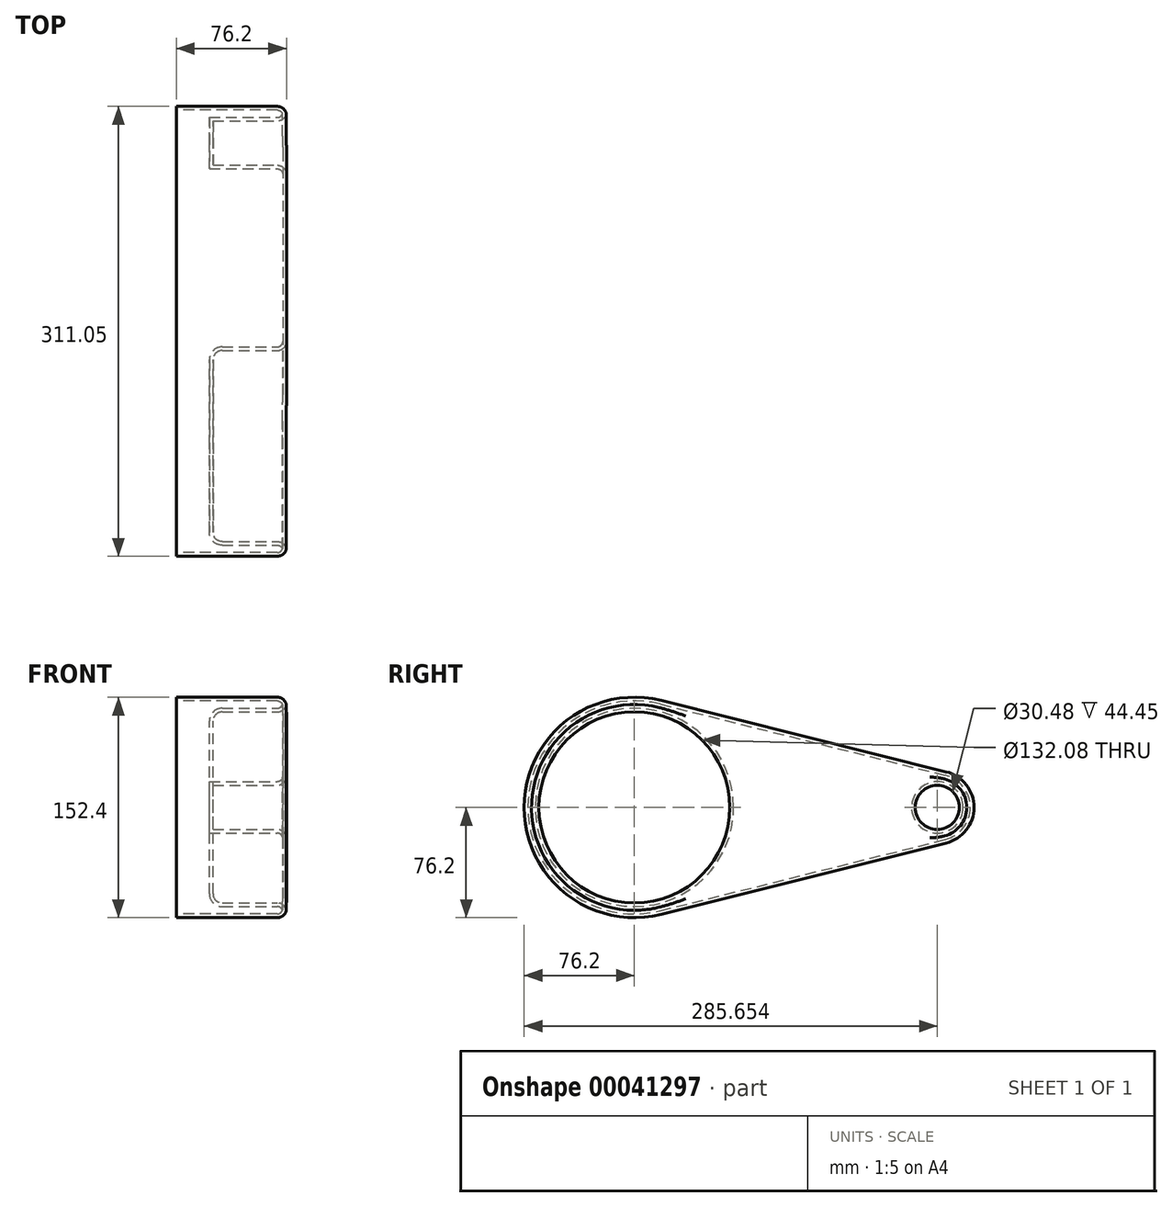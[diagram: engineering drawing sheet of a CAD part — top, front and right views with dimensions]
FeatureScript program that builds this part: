
annotation { "Feature Type Name" : "Feature", "Feature Type Description" : "" }
export const myFeature = defineFeature(function(context is Context, id is Id, definition is map)
    precondition{}
    {
        {
            var Q0;
            Q0=qCreatedBy(makeId("Right.planeOp"),FACE);
            var sketch = newSketch(context, id + "F0", { "sketchPlane" : qUnion([Q0])});
            skCircle(sketch, "E0", {"center": v(0, 0) * mm, "radius": 76.2 * mm});
            skCircle(sketch, "E1", {"center": v(209.45, 0) * mm, "radius": 25.4 * mm});
            skLineSegment(sketch, "E2", {"start": v(18.48, 73.92) * mm, "end": v(215.61, 24.64) * mm});
            skLineSegment(sketch, "E3", {"start": v(18.48, -73.92) * mm, "end": v(215.61, -24.64) * mm});
            skSolve(sketch);
        }
        {
            var Q0;
            {var subQ0=sQuery(id+"F0.wireOp",EDGE,"E0");var subQ2=makeQuery(id+"F0.imprint","INTERSECT",VERTEX,{"derivedFrom":[subQ0,sQuery(id+"F0.wireOp",EDGE,"E2")]});Q0=makeQuery(id+"F0.imprint","IMPRINT",FACE,{"disambiguationData":[TD([[makeQuery(id+"F0.imprint","IMPRINT",EDGE,{"disambiguationData":[TD([[subQ2,-1.0]])],"derivedFrom":subQ0}),1.0]])]});}
            var Q1;
            {var subQ1=sQuery(id+"F0.wireOp",EDGE,"E2");Q1=makeQuery(id+"F0.imprint","IMPRINT",FACE,{"disambiguationData":[TD([[makeQuery(id+"F0.imprint","IMPRINT",EDGE,{"derivedFrom":subQ1}),-1.0]])]});}
            var Q2;
            {var subQ0=sQuery(id+"F0.wireOp",EDGE,"E1");var subQ2=makeQuery(id+"F0.imprint","INTERSECT",VERTEX,{"derivedFrom":[subQ0,sQuery(id+"F0.wireOp",EDGE,"E2")]});Q2=makeQuery(id+"F0.imprint","IMPRINT",FACE,{"disambiguationData":[TD([[makeQuery(id+"F0.imprint","IMPRINT",EDGE,{"disambiguationData":[TD([[subQ2,-1.0]])],"derivedFrom":subQ0}),1.0]])]});}
            extrude(context, id + "F1", {"entities" : qUnion([Q0, Q1, Q2]), "depth" : 76.2 * mm});
        }
        {
            var Q0;
            Q0=makeQuery(id+"F1.opExtrude","CAP_FACE",FACE,{"disambiguationData":[OSD([sQuery(id+"F0.wireOp",EDGE,"E0"),sQuery(id+"F0.wireOp",EDGE,"E1"),sQuery(id+"F0.wireOp",EDGE,"E2"),sQuery(id+"F0.wireOp",EDGE,"E3")])],"isStart":false});
            var sketch = newSketch(context, id + "F2", { "sketchPlane" : qUnion([Q0])});
            skCircle(sketch, "E4", {"center": v(0, 0) * mm, "radius": 66.04 * mm});
            skCircle(sketch, "E5", {"center": v(209.45, 0) * mm, "radius": 15.24 * mm});
            skSolve(sketch);
        }
        {
            var Q0;
            Q0=makeQuery(id+"F2.imprint","IMPRINT",FACE,{"disambiguationData":[TD([[makeQuery(id+"F2.imprint","IMPRINT",EDGE,{"derivedFrom":sQuery(id+"F2.wireOp",EDGE,"E4")}),1.0]])]});
            var Q1;
            Q1=makeQuery(id+"F2.imprint","IMPRINT",FACE,{"disambiguationData":[TD([[makeQuery(id+"F2.imprint","IMPRINT",EDGE,{"derivedFrom":sQuery(id+"F2.wireOp",EDGE,"E5")}),1.0]])]});
            extrude(context, id + "F3", {"entities" : qUnion([Q0, Q1]), "operationType" : NewBodyOperationType.REMOVE, "oppositeDirection" : true, "depth" : 50.8 * mm});
        }
        {
            var Q0;
            Q0=makeQuery(id+"F1.opExtrude","CAP_FACE",FACE,{"disambiguationData":[OSD([sQuery(id+"F0.wireOp",EDGE,"E0"),sQuery(id+"F0.wireOp",EDGE,"E1"),sQuery(id+"F0.wireOp",EDGE,"E2"),sQuery(id+"F0.wireOp",EDGE,"E3")])],"isStart":false});
            var Q1;
            Q1=makeQuery(id+"F3.boolean.opBoolean","COPY",EDGE,{"derivedFrom":makeQuery(id+"F3.opExtrude","CAP_EDGE",EDGE,{"disambiguationData":[OSD([sQuery(id+"F2.wireOp",EDGE,"E4")])],"isStart":false})});
            var Q2;
            Q2=makeQuery(id+"F3.boolean.opBoolean","COPY",EDGE,{"derivedFrom":makeQuery(id+"F3.opExtrude","CAP_EDGE",EDGE,{"disambiguationData":[OSD([sQuery(id+"F2.wireOp",EDGE,"E5")])],"isStart":true})});
            fillet(context, id + "F4", {"entities" : qUnion([Q0, Q1, Q2]), "radius" : 6.35 * mm, "tangentPropagation" : true, "allowEdgeOverflow" : false});
        }
        {
            var Q0;
            Q0=makeQuery(id+"F1.opExtrude","CAP_FACE",FACE,{"disambiguationData":[OSD([sQuery(id+"F0.wireOp",EDGE,"E0"),sQuery(id+"F0.wireOp",EDGE,"E1"),sQuery(id+"F0.wireOp",EDGE,"E2"),sQuery(id+"F0.wireOp",EDGE,"E3")])],"isStart":true});
            shell(context, id + "F5", {"entities" : qUnion([Q0]), "thickness" : 2.54 * mm});
        }
    });
